# Revit family: BDG_BossDesign_Tbls_ATOM_Desks1
name_source: partatom
category: Furniture
revit_build: Autodesk Revit 2016 (Build: 20150220_1215(x64)
units: mm (PartAtom-declared; Revit-internal decimal feet)

## family parameters
Always vertical = Yes
Cut with Voids When Loaded = No
OmniClass Number = 23.40.20.00
OmniClass Title = General Furniture and Specialties
Room Calculation Point = No
Shared = Yes
Work Plane-Based = No

## types (11) — shared parameters
4BayPartitionBetween1&4 = 1000 mm  [stored 3.28084 ft]
Assembly Code = E2020200
AssetType = Movable
BIMObjectName = BDG_BossDesign_Tables_ATOMTables_Desks
Category = Pr_40_50_21 : Desks, tables and worktops
DeskSubSectionLengthMiddleFor3Bay = 1468 mm
DividerLength = 298 mm
DurationUnit = year
ExpectedLife = 5
Finish = Black RAL 9005 or White RAL 9016 Painted Leg Finish or Polished Aluminium
IfcExportAs = IfcFurnishingElementType
IfcExportType = TABLE
IsDeskScreen4 = Yes
IsVerticalUnderFrameLeftEnd = Yes
IsVerticalUnderFrameRightEnd = Yes
Keynote = Pr_40_50_21
ManufacturerName = Boss Design
ManufacturerURL = www.bossdesign.com
Material = Standard Finishes - MFC, MF MDF, Compact Laminate, 
Premium Finishes - Oak & BAW Veneer, Fenix and Linoleum.
NBSDescription = Tables
NBSReference = 45-35-86/327
Name = Tables_ATOMTables_Desks_BossDesign
NominalHeight = 735 mm  [stored 2.41142 ft]
NominalWidth = 1600 mm
OffSetAperture = 300 mm
OffSetFor3BayTableTop = 8079 mm
OffSetForAperture = 300 mm
OffSetForBeam4Bay = 893 mm
ProductInformation = www.bossdesign.com/product-list/atom-tables
URL = www.bossdesign.com
Uniclass2015Code = Pr_40_50_21
Uniclass2015Title = Desks, tables and worktops
Uniclass2015Version = Products v1.10
Version = 1
VerticalPartitionLength = 788 mm
WarrantyDurationLabor = 5
WarrantyDurationParts = 5
WarrantyDurationUnit = year
zero-valued in all types: NumberOfChairs, WorksurfaceArea

## per-type parameters (varying)
- 1500 x 1600mm 2 Person Desk: 2BayHorizontalPartition=788 mm; 3BayPartitionBetween1&3=788 mm; 4BayPartitionsMiddle2Bays=4200 mm; Beam3BayCentralBay=1206 mm; Beam4Bay=1525 mm; BeamBayEnd=1525 mm; CentralPartitionRectangle=1309 mm  [stored 4.29462 ft]; DeskSubSection2&3For4Bay=1400 mm; DeskSubSectionLengthEnd=1800 mm; DeskTopSingular=1500 mm; Is2BayPartition=No; Is2BayPartitionOther=No; Is3BayParitionOther=Yes; Is3BayPartition=No; Is4BayPartition=Yes; Is4BayPartitionOther=Yes; Is4PartitionsBayMiddle2Bays=No; IsCentral2BayFor4Bay=Yes; IsCentral2BayFor4BayOther=Yes; IsCentralBayPartition=No; IsDeskTop1=No; IsDeskTop2=No; IsDeskTop2BayEnds=No; IsDeskTop3=No; IsDeskTop4=No; IsDeskTopSingular=Yes; IsMiddleUnderFrame1Beam=No; IsMiddleUnderFrame2Beam=No; IsMiddleUnderFrame3Beam=No; IsMiddleUnderFrame4Beam=No; IsMiddleUnderFrameSingular=Yes; IsSingularPartition=Yes; IsUnderFrameBeam3BayCentral=Yes; IsVerticalPartition=No; IsVerticalPartition3Bay=No; IsVerticalPartition4Bay=No; IsVerticalUnderFrame3Bay=No; IsVerticalUnderFrame4Bay=No; LongitudinalBeam=1258 mm; Model=BOSS_ATBD15X16; ModelNumber=BOSS_ATBD15X16; NestSet1=Yes; NestSet2=No; NestSet3=No; NominalLength=1500 mm; OffSet2BayBeam=6900 mm; OffSet3BayPartition=500 mm  [stored 1.64042 ft]; OffSet4BeamBayEnd=893 mm; OffSet4Partitions=1320 mm; OffSetApertureEnds=408 mm; OffSetBeam2BayVerticalEnd=8243 mm; OffSetBetweenBeam4Bay=275 mm; OffSetForTableTopEnds=3600 mm; OffSetForVertical3Bay=1280 mm; OffSetForVertical4Bay=1280 mm; OffSetTableTop2Bay=14267 mm; OffsetForUnderFrameEnds=1500 mm; Shape=Rectangular; SingularPartition=1316 mm  [stored 4.31759 ft]; Size=1500 x 1600 x 735mm; TableTop2Bay=1500 mm; TableTopEnds=1112 mm
- 1800 x 1600mm 2 Person Desk: 2BayHorizontalPartition=788 mm; 3BayPartitionBetween1&3=788 mm; 4BayPartitionsMiddle2Bays=4200 mm; Beam3BayCentralBay=1506 mm; Beam4Bay=1525 mm; BeamBayEnd=1525 mm; CentralPartitionRectangle=1616 mm; DeskSubSection2&3For4Bay=1400 mm; DeskSubSectionLengthEnd=1510 mm; DeskTopSingular=1800 mm; Is2BayPartition=No; Is2BayPartitionOther=No; Is3BayParitionOther=Yes; Is3BayPartition=No; Is4BayPartition=Yes; Is4BayPartitionOther=Yes; Is4PartitionsBayMiddle2Bays=No; IsCentral2BayFor4Bay=Yes; IsCentral2BayFor4BayOther=Yes; IsCentralBayPartition=No; IsDeskTop1=No; IsDeskTop2=No; IsDeskTop2BayEnds=No; IsDeskTop3=No; IsDeskTop4=No; IsDeskTopSingular=Yes; IsMiddleUnderFrame1Beam=No; IsMiddleUnderFrame2Beam=No; IsMiddleUnderFrame3Beam=No; IsMiddleUnderFrame4Beam=No; IsMiddleUnderFrameSingular=Yes; IsSingularPartition=Yes; IsUnderFrameBeam3BayCentral=Yes; IsVerticalPartition=No; IsVerticalPartition3Bay=No; IsVerticalPartition4Bay=No; IsVerticalUnderFrame3Bay=No; IsVerticalUnderFrame4Bay=No; LongitudinalBeam=1558 mm; Model=BOSS_ATBD18X16; ModelNumber=BOSS_ATBD18X16; NestSet1=Yes; NestSet2=No; NestSet3=No; NominalLength=1800 mm; OffSet2BayBeam=6900 mm; OffSet3BayPartition=500 mm  [stored 1.64042 ft]; OffSet4BeamBayEnd=900 mm  [stored 2.95276 ft]; OffSet4Partitions=1320 mm; OffSetApertureEnds=558 mm; OffSetBeam2BayVerticalEnd=8243 mm; OffSetBetweenBeam4Bay=275 mm; OffSetForTableTopEnds=3600 mm; OffSetForVertical3Bay=1280 mm; OffSetForVertical4Bay=1280 mm; OffSetTableTop2Bay=14267 mm; OffsetForUnderFrameEnds=1800 mm; Shape=Rectangular; SingularPartition=1616 mm; Size=1800 x 1600 x 735mm; TableTop2Bay=1400 mm; TableTopEnds=1112 mm
- 1600 x 1600mm 2 Person Desk: 2BayHorizontalPartition=788 mm; 3BayPartitionBetween1&3=788 mm; 4BayPartitionsMiddle2Bays=4200 mm; Beam3BayCentralBay=1306 mm  [stored 4.28478 ft]; Beam4Bay=1525 mm; BeamBayEnd=1800 mm; CentralPartitionRectangle=1416 mm; DeskSubSection2&3For4Bay=1400 mm; DeskSubSectionLengthEnd=1799 mm; DeskTopSingular=1600 mm; Is2BayPartition=No; Is2BayPartitionOther=No; Is3BayParitionOther=Yes; Is3BayPartition=No; Is4BayPartition=Yes; Is4BayPartitionOther=Yes; Is4PartitionsBayMiddle2Bays=No; IsCentral2BayFor4Bay=Yes; IsCentral2BayFor4BayOther=Yes; IsCentralBayPartition=No; IsDeskTop1=No; IsDeskTop2=No; IsDeskTop2BayEnds=No; IsDeskTop3=No; IsDeskTop4=No; IsDeskTopSingular=Yes; IsMiddleUnderFrame1Beam=No; IsMiddleUnderFrame2Beam=No; IsMiddleUnderFrame3Beam=No; IsMiddleUnderFrame4Beam=No; IsMiddleUnderFrameSingular=Yes; IsSingularPartition=Yes; IsUnderFrameBeam3BayCentral=Yes; IsVerticalPartition=No; IsVerticalPartition3Bay=No; IsVerticalPartition4Bay=No; IsVerticalUnderFrame3Bay=No; IsVerticalUnderFrame4Bay=No; LongitudinalBeam=1358 mm; Model=BOSS_ATBD16X16; ModelNumber=BOSS_ATBD16X16; NestSet1=Yes; NestSet2=No; NestSet3=No; NominalLength=1600 mm; OffSet2BayBeam=6900 mm; OffSet3BayPartition=500 mm  [stored 1.64042 ft]; OffSet4BeamBayEnd=893 mm; OffSet4Partitions=1320 mm; OffSetApertureEnds=458 mm; OffSetBeam2BayVerticalEnd=8243 mm; OffSetBetweenBeam4Bay=275 mm; OffSetForTableTopEnds=3600 mm; OffSetForVertical3Bay=1280 mm; OffSetForVertical4Bay=1280 mm; OffSetTableTop2Bay=14267 mm; OffsetForUnderFrameEnds=1600 mm; Shape=Square; SingularPartition=1416 mm; Size=1600 x 1600 x 735mm; TableTop2Bay=1400 mm; TableTopEnds=1112 mm
- 2000 x 1600mm 2 Person Desk: 2BayHorizontalPartition=788 mm; 3BayPartitionBetween1&3=788 mm; 4BayPartitionsMiddle2Bays=4200 mm; Beam3BayCentralBay=1706 mm; Beam4Bay=1525 mm; BeamBayEnd=1525 mm; CentralPartitionRectangle=1816 mm; DeskSubSection2&3For4Bay=1400 mm; DeskSubSectionLengthEnd=1799 mm; DeskTopSingular=2000 mm; Is2BayPartition=No; Is2BayPartitionOther=No; Is3BayParitionOther=Yes; Is3BayPartition=No; Is4BayPartition=Yes; Is4BayPartitionOther=Yes; Is4PartitionsBayMiddle2Bays=No; IsCentral2BayFor4Bay=Yes; IsCentral2BayFor4BayOther=Yes; IsCentralBayPartition=No; IsDeskTop1=No; IsDeskTop2=No; IsDeskTop2BayEnds=No; IsDeskTop3=No; IsDeskTop4=No; IsDeskTopSingular=Yes; IsMiddleUnderFrame1Beam=No; IsMiddleUnderFrame2Beam=No; IsMiddleUnderFrame3Beam=No; IsMiddleUnderFrame4Beam=No; IsMiddleUnderFrameSingular=Yes; IsSingularPartition=Yes; IsUnderFrameBeam3BayCentral=Yes; IsVerticalPartition=No; IsVerticalPartition3Bay=No; IsVerticalPartition4Bay=No; IsVerticalUnderFrame3Bay=No; IsVerticalUnderFrame4Bay=No; LongitudinalBeam=1758 mm; Model=BOSS_ATBD20X16; ModelNumber=BOSS_ATBD20X16; NestSet1=Yes; NestSet2=No; NestSet3=No; NominalLength=2000 mm; OffSet2BayBeam=6900 mm; OffSet3BayPartition=500 mm  [stored 1.64042 ft]; OffSet4BeamBayEnd=893 mm; OffSet4Partitions=1320 mm; OffSetApertureEnds=658 mm  [stored 2.15879 ft]; OffSetBeam2BayVerticalEnd=8243 mm; OffSetBetweenBeam4Bay=275 mm; OffSetForTableTopEnds=3600 mm; OffSetForVertical3Bay=1280 mm; OffSetForVertical4Bay=1280 mm; OffSetTableTop2Bay=14267 mm; OffsetForUnderFrameEnds=2000 mm; Shape=Rectangular; SingularPartition=1816 mm; Size=2000 x 1600 x 735mm; TableTop2Bay=1400 mm; TableTopEnds=1112 mm
- 2800 x 1600mm 4 Person Desk: 2BayHorizontalPartition=1308 mm  [stored 4.29134 ft]; 3BayPartitionBetween1&3=788 mm; 4BayPartitionsMiddle2Bays=4200 mm; Beam3BayCentralBay=800 mm  [stored 2.62467 ft]; Beam4Bay=1125 mm; BeamBayEnd=1123 mm  [stored 3.68438 ft]; CentralPartitionRectangle=788 mm; DeskSubSection2&3For4Bay=1400 mm; DeskSubSectionLengthEnd=1400 mm; DeskTopSingular=1400 mm; Is2BayPartition=Yes; Is2BayPartitionOther=No; Is3BayParitionOther=No; Is3BayPartition=No; Is4BayPartition=No; Is4BayPartitionOther=No; Is4PartitionsBayMiddle2Bays=No; IsCentral2BayFor4Bay=Yes; IsCentral2BayFor4BayOther=Yes; IsCentralBayPartition=No; IsDeskTop1=No; IsDeskTop2=No; IsDeskTop2BayEnds=Yes; IsDeskTop3=No; IsDeskTop4=No; IsDeskTopSingular=No; IsMiddleUnderFrame1Beam=Yes; IsMiddleUnderFrame2Beam=No; IsMiddleUnderFrame3Beam=No; IsMiddleUnderFrame4Beam=Yes; IsMiddleUnderFrameSingular=No; IsSingularPartition=No; IsUnderFrameBeam3BayCentral=No; IsVerticalPartition=Yes; IsVerticalPartition3Bay=No; IsVerticalPartition4Bay=No; IsVerticalUnderFrame3Bay=Yes; IsVerticalUnderFrame4Bay=No; LongitudinalBeam=2558 mm; Model=BOSS_ATBD28X16; ModelNumber=BOSS_ATBD28X16; NestSet1=Yes; NestSet2=No; NestSet3=No; NominalLength=2800 mm; OffSet2BayBeam=1253 mm  [stored 4.11089 ft]; OffSet3BayPartition=500 mm  [stored 1.64042 ft]; OffSet4BeamBayEnd=1253 mm  [stored 4.11089 ft]; OffSet4Partitions=1320 mm; OffSetApertureEnds=150 mm; OffSetBeam2BayVerticalEnd=8243 mm; OffSetBetweenBeam4Bay=260 mm  [stored 0.853018 ft]; OffSetForTableTopEnds=3600 mm; OffSetForVertical3Bay=1280 mm; OffSetForVertical4Bay=1280 mm; OffSetTableTop2Bay=1400 mm; OffsetForUnderFrameEnds=2800 mm; Shape=Rectangular; SingularPartition=500 mm  [stored 1.64042 ft]; Size=2800 x 1600 x 735mm; TableTop2Bay=1400 mm; TableTopEnds=1112 mm
- 3600 x 1600mm 4 Person Desk: 2BayHorizontalPartition=1704 mm; 3BayPartitionBetween1&3=788 mm; 4BayPartitionsMiddle2Bays=4200 mm; Beam3BayCentralBay=1523 mm; Beam4Bay=1523 mm; BeamBayEnd=1523 mm; CentralPartitionRectangle=788 mm; DeskSubSection2&3For4Bay=1800 mm; DeskSubSectionLengthEnd=1800 mm; DeskTopSingular=1800 mm; Is2BayPartition=No; Is2BayPartitionOther=Yes; Is3BayParitionOther=No; Is3BayPartition=No; Is4BayPartition=Yes; Is4BayPartitionOther=Yes; Is4PartitionsBayMiddle2Bays=No; IsCentral2BayFor4Bay=Yes; IsCentral2BayFor4BayOther=Yes; IsCentralBayPartition=No; IsDeskTop1=No; IsDeskTop2=No; IsDeskTop2BayEnds=Yes; IsDeskTop3=No; IsDeskTop4=No; IsDeskTopSingular=No; IsMiddleUnderFrame1Beam=Yes; IsMiddleUnderFrame2Beam=No; IsMiddleUnderFrame3Beam=No; IsMiddleUnderFrame4Beam=Yes; IsMiddleUnderFrameSingular=No; IsSingularPartition=No; IsUnderFrameBeam3BayCentral=No; IsVerticalPartition=Yes; IsVerticalPartition3Bay=No; IsVerticalPartition4Bay=No; IsVerticalUnderFrame3Bay=Yes; IsVerticalUnderFrame4Bay=No; LongitudinalBeam=3358 mm; Model=BOSS_ATBD36X16; ModelNumber=BOSS_ATBD36X16; NestSet1=Yes; NestSet2=Yes; NestSet3=No; NominalLength=3600 mm; OffSet2BayBeam=1653 mm; OffSet3BayPartition=500 mm  [stored 1.64042 ft]; OffSet4BeamBayEnd=1800 mm; OffSet4Partitions=1320 mm; OffSetApertureEnds=150 mm; OffSetBeam2BayVerticalEnd=1800 mm; OffSetBetweenBeam4Bay=260 mm  [stored 0.853018 ft]; OffSetForTableTopEnds=3600 mm; OffSetForVertical3Bay=1280 mm; OffSetForVertical4Bay=1280 mm; OffSetTableTop2Bay=1800 mm; OffsetForUnderFrameEnds=3600 mm; Shape=Rectangular; SingularPartition=500 mm  [stored 1.64042 ft]; Size=3600 x 1600 x 735mm; TableTop2Bay=1800 mm; TableTopEnds=1112 mm
- 4200 x 1600mm 6 Person Desk: 2BayHorizontalPartition=788 mm; 3BayPartitionBetween1&3=1308 mm  [stored 4.29134 ft]; 4BayPartitionsMiddle2Bays=4200 mm; Beam3BayCentralBay=1140 mm  [stored 3.74016 ft]; Beam4Bay=1140 mm  [stored 3.74016 ft]; BeamBayEnd=1123 mm  [stored 3.68438 ft]; CentralPartitionRectangle=1400 mm; DeskSubSection2&3For4Bay=700 mm  [stored 2.29659 ft]; DeskSubSectionLengthEnd=1800 mm; DeskTopSingular=1400 mm; Is2BayPartition=No; Is2BayPartitionOther=No; Is3BayParitionOther=Yes; Is3BayPartition=No; Is4BayPartition=No; Is4BayPartitionOther=No; Is4PartitionsBayMiddle2Bays=No; IsCentral2BayFor4Bay=No; IsCentral2BayFor4BayOther=No; IsCentralBayPartition=Yes; IsDeskTop1=Yes; IsDeskTop2=No; IsDeskTop2BayEnds=No; IsDeskTop3=No; IsDeskTop4=Yes; IsDeskTopSingular=Yes; IsMiddleUnderFrame1Beam=Yes; IsMiddleUnderFrame2Beam=No; IsMiddleUnderFrame3Beam=No; IsMiddleUnderFrame4Beam=Yes; IsMiddleUnderFrameSingular=No; IsSingularPartition=No; IsUnderFrameBeam3BayCentral=Yes; IsVerticalPartition=No; IsVerticalPartition3Bay=Yes; IsVerticalPartition4Bay=No; IsVerticalUnderFrame3Bay=No; IsVerticalUnderFrame4Bay=Yes; LongitudinalBeam=3958 mm; Model=BOSS_ATBD42X16; ModelNumber=BOSS_ATBD42X16; NestSet1=No; NestSet2=Yes; NestSet3=No; NominalLength=4200 mm; OffSet2BayBeam=1955 mm; OffSet3BayPartition=700 mm  [stored 2.29659 ft]; OffSet4BeamBayEnd=1800 mm; OffSet4Partitions=1320 mm; OffSetApertureEnds=150 mm; OffSetBeam2BayVerticalEnd=1800 mm; OffSetBetweenBeam4Bay=1953 mm; OffSetForTableTopEnds=2100 mm; OffSetForVertical3Bay=680 mm  [stored 2.23097 ft]; OffSetForVertical4Bay=1280 mm; OffSetTableTop2Bay=1800 mm; OffsetForUnderFrameEnds=4200 mm; Shape=Rectangular; SingularPartition=500 mm  [stored 1.64042 ft]; Size=4200 x 1600 x 735mm; TableTop2Bay=1400 mm; TableTopEnds=1400 mm
- 1400 x 1600mm 2 Person Desk: 2BayHorizontalPartition=788 mm; 3BayPartitionBetween1&3=788 mm; 4BayPartitionsMiddle2Bays=4200 mm; Beam3BayCentralBay=1106 mm  [stored 3.62861 ft]; Beam4Bay=1525 mm; BeamBayEnd=1525 mm; CentralPartitionRectangle=1216 mm  [stored 3.9895 ft]; DeskSubSection2&3For4Bay=1400 mm; DeskSubSectionLengthEnd=1800 mm; DeskTopSingular=1400 mm; Is2BayPartition=No; Is2BayPartitionOther=No; Is3BayParitionOther=Yes; Is3BayPartition=No; Is4BayPartition=Yes; Is4BayPartitionOther=Yes; Is4PartitionsBayMiddle2Bays=No; IsCentral2BayFor4Bay=Yes; IsCentral2BayFor4BayOther=Yes; IsCentralBayPartition=No; IsDeskTop1=No; IsDeskTop2=No; IsDeskTop2BayEnds=No; IsDeskTop3=No; IsDeskTop4=No; IsDeskTopSingular=Yes; IsMiddleUnderFrame1Beam=No; IsMiddleUnderFrame2Beam=No; IsMiddleUnderFrame3Beam=No; IsMiddleUnderFrame4Beam=No; IsMiddleUnderFrameSingular=Yes; IsSingularPartition=Yes; IsUnderFrameBeam3BayCentral=Yes; IsVerticalPartition=No; IsVerticalPartition3Bay=No; IsVerticalPartition4Bay=No; IsVerticalUnderFrame3Bay=No; IsVerticalUnderFrame4Bay=No; LongitudinalBeam=1158 mm  [stored 3.79921 ft]; Model=BOSS_ATBD14X16; ModelNumber=BOSS_ATBD14X16; NestSet1=Yes; NestSet2=No; NestSet3=No; NominalLength=1400 mm; OffSet2BayBeam=6900 mm; OffSet3BayPartition=500 mm  [stored 1.64042 ft]; OffSet4BeamBayEnd=893 mm; OffSet4Partitions=1320 mm; OffSetApertureEnds=358 mm  [stored 1.17454 ft]; OffSetBeam2BayVerticalEnd=8243 mm; OffSetBetweenBeam4Bay=275 mm; OffSetForTableTopEnds=3600 mm; OffSetForVertical3Bay=1280 mm; OffSetForVertical4Bay=1280 mm; OffSetTableTop2Bay=14267 mm; OffsetForUnderFrameEnds=1400 mm; Shape=Rectangular; SingularPartition=1216 mm  [stored 3.9895 ft]; Size=1400 x 1600 x 735mm; TableTop2Bay=1400 mm; TableTopEnds=1112 mm
- 5400 x 1600mm 6 Person Desk: 2BayHorizontalPartition=788 mm; 3BayPartitionBetween1&3=1708 mm; 4BayPartitionsMiddle2Bays=1800 mm; Beam3BayCentralBay=1540 mm; Beam4Bay=1540 mm; BeamBayEnd=1523 mm; CentralPartitionRectangle=1800 mm; DeskSubSection2&3For4Bay=900 mm  [stored 2.95276 ft]; DeskSubSectionLengthEnd=1800 mm; DeskTopSingular=1800 mm; Is2BayPartition=No; Is2BayPartitionOther=No; Is3BayParitionOther=No; Is3BayPartition=Yes; Is4BayPartition=No; Is4BayPartitionOther=No; Is4PartitionsBayMiddle2Bays=No; IsCentral2BayFor4Bay=No; IsCentral2BayFor4BayOther=No; IsCentralBayPartition=Yes; IsDeskTop1=Yes; IsDeskTop2=No; IsDeskTop2BayEnds=No; IsDeskTop3=No; IsDeskTop4=Yes; IsDeskTopSingular=Yes; IsMiddleUnderFrame1Beam=Yes; IsMiddleUnderFrame2Beam=No; IsMiddleUnderFrame3Beam=No; IsMiddleUnderFrame4Beam=Yes; IsMiddleUnderFrameSingular=No; IsSingularPartition=No; IsUnderFrameBeam3BayCentral=Yes; IsVerticalPartition=No; IsVerticalPartition3Bay=Yes; IsVerticalPartition4Bay=No; IsVerticalUnderFrame3Bay=No; IsVerticalUnderFrame4Bay=Yes; LongitudinalBeam=5158 mm; Model=BOSS_ATBD54X16; ModelNumber=BOSS_ATBD54X16; NestSet1=No; NestSet2=Yes; NestSet3=No; NominalLength=5400 mm; OffSet2BayBeam=2553 mm; OffSet3BayPartition=900 mm  [stored 2.95276 ft]; OffSet4BeamBayEnd=1800 mm; OffSet4Partitions=1320 mm; OffSetApertureEnds=150 mm; OffSetBeam2BayVerticalEnd=1800 mm; OffSetBetweenBeam4Bay=770 mm  [stored 2.52625 ft]; OffSetForTableTopEnds=2700 mm; OffSetForVertical3Bay=880 mm  [stored 2.88714 ft]; OffSetForVertical4Bay=1780 mm; OffSetTableTop2Bay=2700 mm; OffsetForUnderFrameEnds=5400 mm; Shape=Rectangular; SingularPartition=500 mm  [stored 1.64042 ft]; Size=5400 x 1600 x 735mm; TableTop2Bay=1800 mm; TableTopEnds=1800 mm
- 5600 x 1600mm 8 Person Desk: 2BayHorizontalPartition=788 mm; 3BayPartitionBetween1&3=1308 mm  [stored 4.29134 ft]; 4BayPartitionsMiddle2Bays=1400 mm; Beam3BayCentralBay=800 mm  [stored 2.62467 ft]; Beam4Bay=1140 mm  [stored 3.74016 ft]; BeamBayEnd=1125 mm; CentralPartitionRectangle=788 mm; DeskSubSection2&3For4Bay=1400 mm; DeskSubSectionLengthEnd=1800 mm; DeskTopSingular=1400 mm; Is2BayPartition=No; Is2BayPartitionOther=No; Is3BayParitionOther=No; Is3BayPartition=No; Is4BayPartition=Yes; Is4BayPartitionOther=No; Is4PartitionsBayMiddle2Bays=Yes; IsCentral2BayFor4Bay=Yes; IsCentral2BayFor4BayOther=No; IsCentralBayPartition=No; IsDeskTop1=Yes; IsDeskTop2=Yes; IsDeskTop2BayEnds=No; IsDeskTop3=Yes; IsDeskTop4=Yes; IsDeskTopSingular=No; IsMiddleUnderFrame1Beam=Yes; IsMiddleUnderFrame2Beam=Yes; IsMiddleUnderFrame3Beam=Yes; IsMiddleUnderFrame4Beam=Yes; IsMiddleUnderFrameSingular=No; IsSingularPartition=No; IsUnderFrameBeam3BayCentral=No; IsVerticalPartition=No; IsVerticalPartition3Bay=No; IsVerticalPartition4Bay=Yes; IsVerticalUnderFrame3Bay=Yes; IsVerticalUnderFrame4Bay=Yes; LongitudinalBeam=5358 mm; Model=BOSS_ATBD56X16; ModelNumber=BOSS_ATBD56X16; NestSet1=No; NestSet2=No; NestSet3=Yes; NominalLength=5600 mm; OffSet2BayBeam=2653 mm; OffSet3BayPartition=1400 mm; OffSet4BeamBayEnd=1270 mm; OffSet4Partitions=0 mm  [stored 0 ft]; OffSetApertureEnds=150 mm; OffSetBeam2BayVerticalEnd=1400 mm; OffSetBetweenBeam4Bay=1270 mm; OffSetForTableTopEnds=2800 mm; OffSetForVertical3Bay=1280 mm; OffSetForVertical4Bay=1380 mm; OffSetTableTop2Bay=2800 mm; OffsetForUnderFrameEnds=5600 mm; Shape=Rectangular; SingularPartition=500 mm  [stored 1.64042 ft]; Size=5600 x 1600 x 735mm; TableTop2Bay=1400 mm; TableTopEnds=1400 mm
- 7200 x 1600mm 8 Person Desk: 2BayHorizontalPartition=788 mm; 3BayPartitionBetween1&3=1708 mm; 4BayPartitionsMiddle2Bays=1800 mm; Beam3BayCentralBay=800 mm  [stored 2.62467 ft]; Beam4Bay=1540 mm; BeamBayEnd=1523 mm; CentralPartitionRectangle=788 mm; DeskSubSection2&3For4Bay=1800 mm; DeskSubSectionLengthEnd=1800 mm; DeskTopSingular=1800 mm; Is2BayPartition=No; Is2BayPartitionOther=No; Is3BayParitionOther=No; Is3BayPartition=No; Is4BayPartition=No; Is4BayPartitionOther=Yes; Is4PartitionsBayMiddle2Bays=Yes; IsCentral2BayFor4Bay=No; IsCentral2BayFor4BayOther=Yes; IsCentralBayPartition=No; IsDeskTop1=Yes; IsDeskTop2=Yes; IsDeskTop2BayEnds=No; IsDeskTop3=Yes; IsDeskTop4=Yes; IsDeskTopSingular=No; IsMiddleUnderFrame1Beam=Yes; IsMiddleUnderFrame2Beam=Yes; IsMiddleUnderFrame3Beam=Yes; IsMiddleUnderFrame4Beam=Yes; IsMiddleUnderFrameSingular=No; IsSingularPartition=No; IsUnderFrameBeam3BayCentral=No; IsVerticalPartition=Yes; IsVerticalPartition3Bay=No; IsVerticalPartition4Bay=Yes; IsVerticalUnderFrame3Bay=Yes; IsVerticalUnderFrame4Bay=Yes; LongitudinalBeam=6958 mm; Model=BOSS_ATBD72X16; ModelNumber=BOSS_ATBD72X16; NestSet1=No; NestSet2=No; NestSet3=Yes; NominalLength=7200 mm; OffSet2BayBeam=3453 mm; OffSet3BayPartition=1800 mm; OffSet4BeamBayEnd=1800 mm; OffSet4Partitions=1320 mm; OffSetApertureEnds=150 mm; OffSetBeam2BayVerticalEnd=1800 mm; OffSetBetweenBeam4Bay=1670 mm; OffSetForTableTopEnds=3600 mm; OffSetForVertical3Bay=1280 mm; OffSetForVertical4Bay=1780 mm; OffSetTableTop2Bay=2800 mm; OffsetForUnderFrameEnds=7200 mm; Shape=Rectangular; SingularPartition=500 mm  [stored 1.64042 ft]; Size=7200 x 1600 x 735mm; TableTop2Bay=1800 mm; TableTopEnds=1800 mm

note: column(s) folded — value = type name in every type: Description, ModelReference

note: [stored X ft] marks values corroborated as IEEE doubles in the binary element streams (Revit-internal decimal feet)

## geometry (parser evidence)
native form markers: Sweep x13
no freeform markers — native parametric forms only
